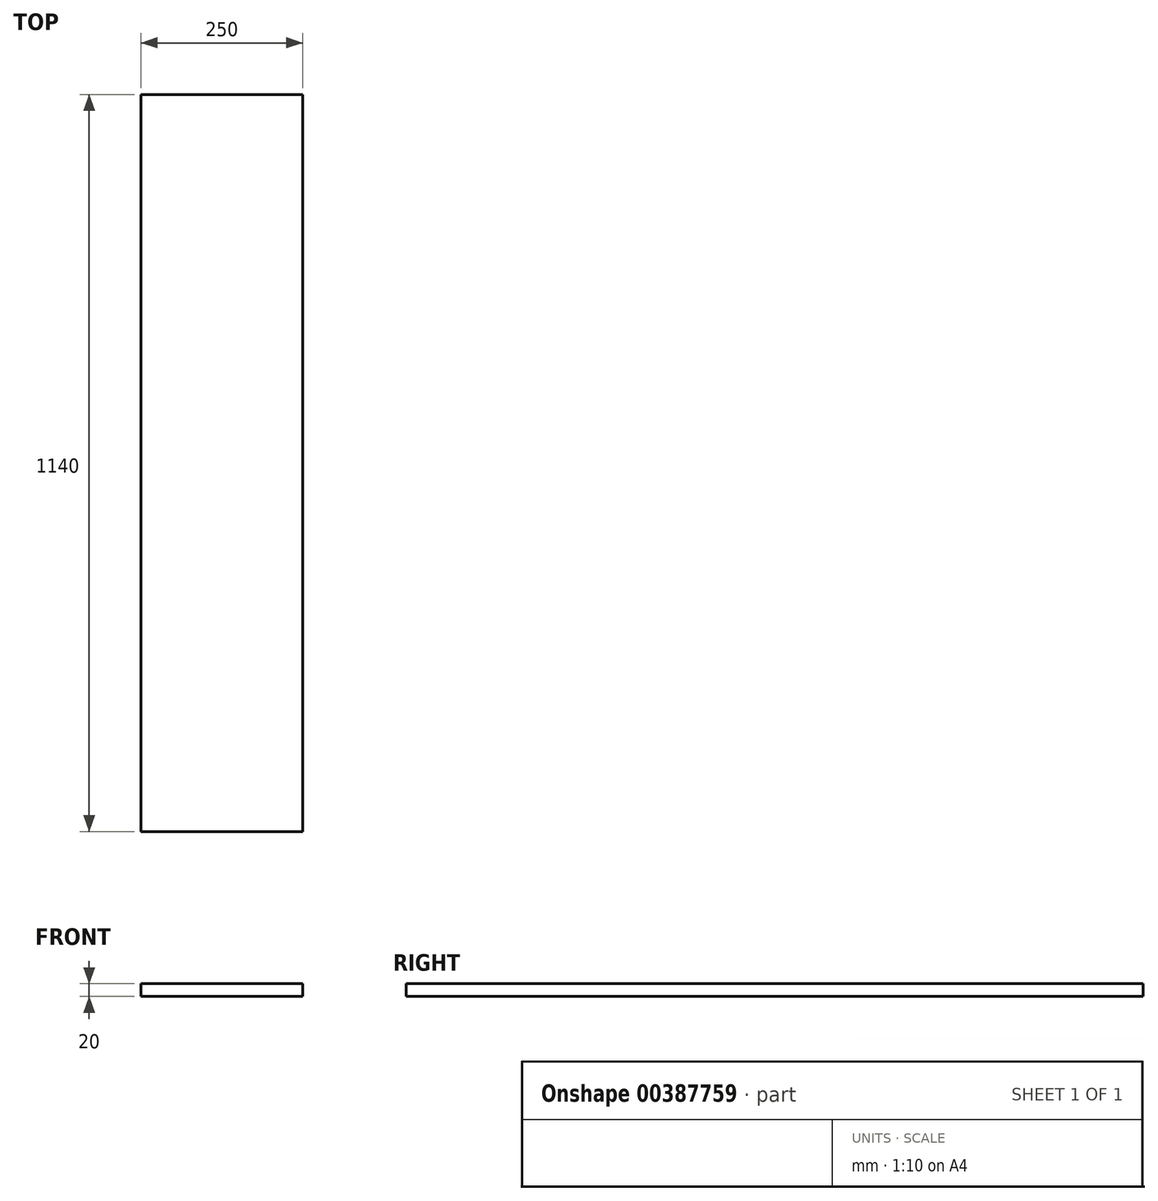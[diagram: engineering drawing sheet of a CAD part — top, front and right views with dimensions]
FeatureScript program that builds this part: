
annotation { "Feature Type Name" : "Feature", "Feature Type Description" : "" }
export const myFeature = defineFeature(function(context is Context, id is Id, definition is map)
    precondition{}
    {
        {
            var Q0;
            Q0=qCreatedBy(makeId("Top.planeOp"),FACE);
            var sketch = newSketch(context, id + "F0", { "sketchPlane" : qUnion([Q0])});
            skLineSegment(sketch, "E0.bottom", {"start": v(0, 0) * mm, "end": v(250, 0) * mm});
            skLineSegment(sketch, "E0.top", {"start": v(0, 1140) * mm, "end": v(250, 1140) * mm});
            skLineSegment(sketch, "E0.left", {"start": v(0, 0) * mm, "end": v(0, 1140) * mm});
            skLineSegment(sketch, "E0.right", {"start": v(250, 0) * mm, "end": v(250, 1140) * mm});
            skSolve(sketch);
        }
        {
            var Q0;
            Q0=makeQuery(id+"F0.imprint","IMPRINT",FACE,{"disambiguationData":[TD([[makeQuery(id+"F0.imprint","IMPRINT",EDGE,{"derivedFrom":sQuery(id+"F0.wireOp",EDGE,"E0.bottom")}),1.0]])]});
            extrude(context, id + "F1", {"entities" : qUnion([Q0]), "depth" : 20 * mm});
        }
    });
